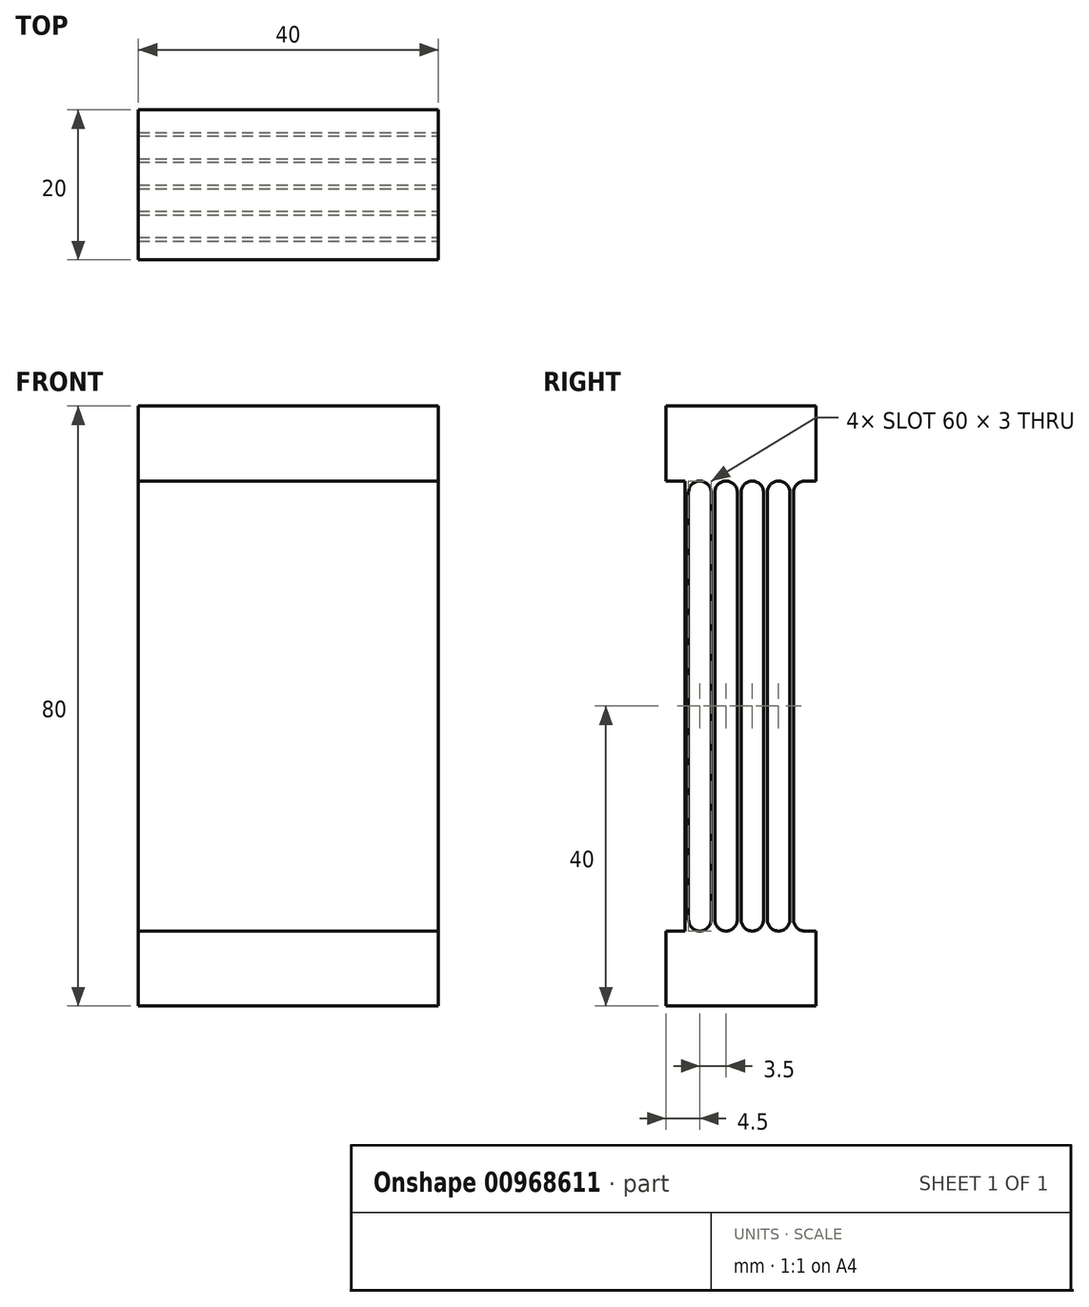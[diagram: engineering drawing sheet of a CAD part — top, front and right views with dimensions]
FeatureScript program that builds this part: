
annotation { "Feature Type Name" : "Feature", "Feature Type Description" : "" }
export const myFeature = defineFeature(function(context is Context, id is Id, definition is map)
    precondition{}
    {
        {
            var Q0;
            Q0=qCreatedBy(makeId("Top.planeOp"),FACE);
            var sketch = newSketch(context, id + "F0", { "sketchPlane" : qUnion([Q0])});
            skLineSegment(sketch, "E0.bottom", {"start": v(0, 0) * mm, "end": v(40, 0) * mm});
            skLineSegment(sketch, "E0.top", {"start": v(0, -20) * mm, "end": v(40, -20) * mm});
            skLineSegment(sketch, "E0.left", {"start": v(0, 0) * mm, "end": v(0, -20) * mm});
            skLineSegment(sketch, "E0.right", {"start": v(40, 0) * mm, "end": v(40, -20) * mm});
            skSolve(sketch);
        }
        {
            var Q0;
            Q0=makeQuery(id+"F0.imprint","IMPRINT",FACE,{"disambiguationData":[TD([[makeQuery(id+"F0.imprint","IMPRINT",EDGE,{"derivedFrom":sQuery(id+"F0.wireOp",EDGE,"E0.bottom")}),-1.0]])]});
            extrude(context, id + "F1", {"entities" : qUnion([Q0]), "depth" : 10 * mm, "offsetDistance" : 25 * mm});
        }
        {
            assignVariable(context, id + "F2", {"name" : "plateSeperation", "anyValue" : 3 * mm});
        }
        {
            var Q0;
            Q0=makeQuery(id+"F1.opExtrude","CAP_FACE",FACE,{"disambiguationData":[OSD([sQuery(id+"F0.wireOp",EDGE,"E0.bottom"),sQuery(id+"F0.wireOp",EDGE,"E0.top"),sQuery(id+"F0.wireOp",EDGE,"E0.left"),sQuery(id+"F0.wireOp",EDGE,"E0.right")])],"isStart":false});
            var sketch = newSketch(context, id + "F3", { "sketchPlane" : qUnion([Q0])});
            skLineSegment(sketch, "E1.bottom", {"start": v(0, -3) * mm, "end": v(40, -3) * mm});
            skLineSegment(sketch, "E1.top", {"start": v(0, -3.5) * mm, "end": v(40, -3.5) * mm});
            skLineSegment(sketch, "E1.left", {"start": v(0, -3) * mm, "end": v(0, -3.5) * mm});
            skLineSegment(sketch, "E1.right", {"start": v(40, -3) * mm, "end": v(40, -3.5) * mm});
            skLineSegment(sketch, "E2.bottom", {"start": v(0, -6.5) * mm, "end": v(40, -6.5) * mm});
            skLineSegment(sketch, "E2.top", {"start": v(0, -7) * mm, "end": v(40, -7) * mm});
            skLineSegment(sketch, "E2.left", {"start": v(0, -6.5) * mm, "end": v(0, -7) * mm});
            skLineSegment(sketch, "E2.right", {"start": v(40, -6.5) * mm, "end": v(40, -7) * mm});
            skLineSegment(sketch, "E3.bottom", {"start": v(0, -10) * mm, "end": v(40, -10) * mm});
            skLineSegment(sketch, "E3.top", {"start": v(0, -10.5) * mm, "end": v(40, -10.5) * mm});
            skLineSegment(sketch, "E3.left", {"start": v(0, -10) * mm, "end": v(0, -10.5) * mm});
            skLineSegment(sketch, "E3.right", {"start": v(40, -10) * mm, "end": v(40, -10.5) * mm});
            skLineSegment(sketch, "E4.bottom", {"start": v(0, -13.5) * mm, "end": v(40, -13.5) * mm});
            skLineSegment(sketch, "E4.top", {"start": v(0, -14) * mm, "end": v(40, -14) * mm});
            skLineSegment(sketch, "E4.left", {"start": v(0, -13.5) * mm, "end": v(0, -14) * mm});
            skLineSegment(sketch, "E4.right", {"start": v(40, -13.5) * mm, "end": v(40, -14) * mm});
            skLineSegment(sketch, "E5.bottom", {"start": v(0, -17) * mm, "end": v(40, -17) * mm});
            skLineSegment(sketch, "E5.top", {"start": v(0, -17.5) * mm, "end": v(40, -17.5) * mm});
            skLineSegment(sketch, "E5.left", {"start": v(0, -17) * mm, "end": v(0, -17.5) * mm});
            skLineSegment(sketch, "E5.right", {"start": v(40, -17) * mm, "end": v(40, -17.5) * mm});
            skSolve(sketch);
        }
        {
            var Q0;
            Q0=makeQuery(id+"F3.imprint","IMPRINT",FACE,{"disambiguationData":[TD([[makeQuery(id+"F3.imprint","IMPRINT",EDGE,{"derivedFrom":sQuery(id+"F3.wireOp",EDGE,"E1.bottom")}),-1.0]])]});
            var Q1;
            Q1=makeQuery(id+"F3.imprint","IMPRINT",FACE,{"disambiguationData":[TD([[makeQuery(id+"F3.imprint","IMPRINT",EDGE,{"derivedFrom":sQuery(id+"F3.wireOp",EDGE,"E2.bottom")}),-1.0]])]});
            var Q2;
            Q2=makeQuery(id+"F3.imprint","IMPRINT",FACE,{"disambiguationData":[TD([[makeQuery(id+"F3.imprint","IMPRINT",EDGE,{"derivedFrom":sQuery(id+"F3.wireOp",EDGE,"E3.bottom")}),-1.0]])]});
            var Q3;
            Q3=makeQuery(id+"F3.imprint","IMPRINT",FACE,{"disambiguationData":[TD([[makeQuery(id+"F3.imprint","IMPRINT",EDGE,{"derivedFrom":sQuery(id+"F3.wireOp",EDGE,"E4.bottom")}),-1.0]])]});
            var Q4;
            Q4=makeQuery(id+"F3.imprint","IMPRINT",FACE,{"disambiguationData":[TD([[makeQuery(id+"F3.imprint","IMPRINT",EDGE,{"derivedFrom":sQuery(id+"F3.wireOp",EDGE,"E5.bottom")}),-1.0]])]});
            extrude(context, id + "F4", {"entities" : qUnion([Q0, Q1, Q2, Q3, Q4]), "operationType" : NewBodyOperationType.ADD, "depth" : 30 * mm, "offsetDistance" : 25 * mm});
        }
        {
            var Q0;
            Q0=makeQuery(id+"F1.opExtrude","SWEPT_BODY",BODY,{"disambiguationData":[OSD([sQuery(id+"F0.wireOp",EDGE,"E0.bottom"),sQuery(id+"F0.wireOp",EDGE,"E0.top"),sQuery(id+"F0.wireOp",EDGE,"E0.left"),sQuery(id+"F0.wireOp",EDGE,"E0.right")])]});
            var Q1;
            Q1=makeQuery(id+"F4.opExtrude","CAP_FACE",FACE,{"disambiguationData":[OSD([sQuery(id+"F3.wireOp",EDGE,"E5.bottom"),sQuery(id+"F3.wireOp",EDGE,"E5.top"),sQuery(id+"F3.wireOp",EDGE,"E5.left"),sQuery(id+"F3.wireOp",EDGE,"E5.right")])],"isStart":false});
            mirror(context, id + "F5", {"operationType" : NewBodyOperationType.ADD, "entities" : qUnion([Q0]), "mirrorPlane" : qUnion([Q1])});
        }
        {
            var Q0;
            Q0=makeQuery(id+"F5.opPattern","COPY",EDGE,{"derivedFrom":makeQuery(id+"F4.opExtrude","CAP_EDGE",EDGE,{"disambiguationData":[OSD([sQuery(id+"F3.wireOp",EDGE,"E5.bottom")])],"isStart":true}),"instanceName":"1"});
            var Q1;
            Q1=makeQuery(id+"F5.opPattern","COPY",EDGE,{"derivedFrom":makeQuery(id+"F4.opExtrude","CAP_EDGE",EDGE,{"disambiguationData":[OSD([sQuery(id+"F3.wireOp",EDGE,"E4.bottom")])],"isStart":true}),"instanceName":"1"});
            var Q2;
            Q2=makeQuery(id+"F5.opPattern","COPY",EDGE,{"derivedFrom":makeQuery(id+"F4.opExtrude","CAP_EDGE",EDGE,{"disambiguationData":[OSD([sQuery(id+"F3.wireOp",EDGE,"E3.bottom")])],"isStart":true}),"instanceName":"1"});
            var Q3;
            Q3=makeQuery(id+"F5.opPattern","COPY",EDGE,{"derivedFrom":makeQuery(id+"F4.opExtrude","CAP_EDGE",EDGE,{"disambiguationData":[OSD([sQuery(id+"F3.wireOp",EDGE,"E2.bottom")])],"isStart":true}),"instanceName":"1"});
            var Q4;
            Q4=makeQuery(id+"F5.opPattern","COPY",EDGE,{"derivedFrom":makeQuery(id+"F4.opExtrude","CAP_EDGE",EDGE,{"disambiguationData":[OSD([sQuery(id+"F3.wireOp",EDGE,"E1.bottom")])],"isStart":true}),"instanceName":"1"});
            var Q5;
            Q5=makeQuery(id+"F5.opPattern","COPY",EDGE,{"derivedFrom":makeQuery(id+"F4.opExtrude","CAP_EDGE",EDGE,{"disambiguationData":[OSD([sQuery(id+"F3.wireOp",EDGE,"E1.top")])],"isStart":true}),"instanceName":"1"});
            var Q6;
            Q6=makeQuery(id+"F5.opPattern","COPY",EDGE,{"derivedFrom":makeQuery(id+"F4.opExtrude","CAP_EDGE",EDGE,{"disambiguationData":[OSD([sQuery(id+"F3.wireOp",EDGE,"E2.top")])],"isStart":true}),"instanceName":"1"});
            var Q7;
            Q7=makeQuery(id+"F5.opPattern","COPY",EDGE,{"derivedFrom":makeQuery(id+"F4.opExtrude","CAP_EDGE",EDGE,{"disambiguationData":[OSD([sQuery(id+"F3.wireOp",EDGE,"E3.top")])],"isStart":true}),"instanceName":"1"});
            var Q8;
            Q8=makeQuery(id+"F5.opPattern","COPY",EDGE,{"derivedFrom":makeQuery(id+"F4.opExtrude","CAP_EDGE",EDGE,{"disambiguationData":[OSD([sQuery(id+"F3.wireOp",EDGE,"E4.top")])],"isStart":true}),"instanceName":"1"});
            var Q9;
            Q9=makeQuery(id+"F5.opPattern","COPY",EDGE,{"derivedFrom":makeQuery(id+"F4.opExtrude","CAP_EDGE",EDGE,{"disambiguationData":[OSD([sQuery(id+"F3.wireOp",EDGE,"E5.top")])],"isStart":true}),"instanceName":"1"});
            var Q10;
            Q10=makeQuery(id+"F4.opExtrude","CAP_EDGE",EDGE,{"disambiguationData":[OSD([sQuery(id+"F3.wireOp",EDGE,"E5.top")])],"isStart":true});
            var Q11;
            Q11=makeQuery(id+"F4.opExtrude","CAP_EDGE",EDGE,{"disambiguationData":[OSD([sQuery(id+"F3.wireOp",EDGE,"E4.top")])],"isStart":true});
            var Q12;
            Q12=makeQuery(id+"F4.opExtrude","CAP_EDGE",EDGE,{"disambiguationData":[OSD([sQuery(id+"F3.wireOp",EDGE,"E3.top")])],"isStart":true});
            var Q13;
            Q13=makeQuery(id+"F4.opExtrude","CAP_EDGE",EDGE,{"disambiguationData":[OSD([sQuery(id+"F3.wireOp",EDGE,"E2.top")])],"isStart":true});
            var Q14;
            Q14=makeQuery(id+"F4.opExtrude","CAP_EDGE",EDGE,{"disambiguationData":[OSD([sQuery(id+"F3.wireOp",EDGE,"E1.top")])],"isStart":true});
            var Q15;
            Q15=makeQuery(id+"F4.opExtrude","CAP_EDGE",EDGE,{"disambiguationData":[OSD([sQuery(id+"F3.wireOp",EDGE,"E5.bottom")])],"isStart":true});
            var Q16;
            Q16=makeQuery(id+"F4.opExtrude","CAP_EDGE",EDGE,{"disambiguationData":[OSD([sQuery(id+"F3.wireOp",EDGE,"E4.bottom")])],"isStart":true});
            var Q17;
            Q17=makeQuery(id+"F4.opExtrude","CAP_EDGE",EDGE,{"disambiguationData":[OSD([sQuery(id+"F3.wireOp",EDGE,"E3.bottom")])],"isStart":true});
            var Q18;
            Q18=makeQuery(id+"F4.opExtrude","CAP_EDGE",EDGE,{"disambiguationData":[OSD([sQuery(id+"F3.wireOp",EDGE,"E2.bottom")])],"isStart":true});
            var Q19;
            Q19=makeQuery(id+"F4.opExtrude","CAP_EDGE",EDGE,{"disambiguationData":[OSD([sQuery(id+"F3.wireOp",EDGE,"E1.bottom")])],"isStart":true});
            fillet(context, id + "F6", {"entities" : qUnion([Q0, Q1, Q2, Q3, Q4, Q5, Q6, Q7, Q8, Q9, Q10, Q11, Q12, Q13, Q14, Q15, Q16, Q17, Q18, Q19]), "radius" : getVariable(context, 'plateSeperation') / 2, "tangentPropagation" : true, "allowEdgeOverflow" : false});
        }
    });
